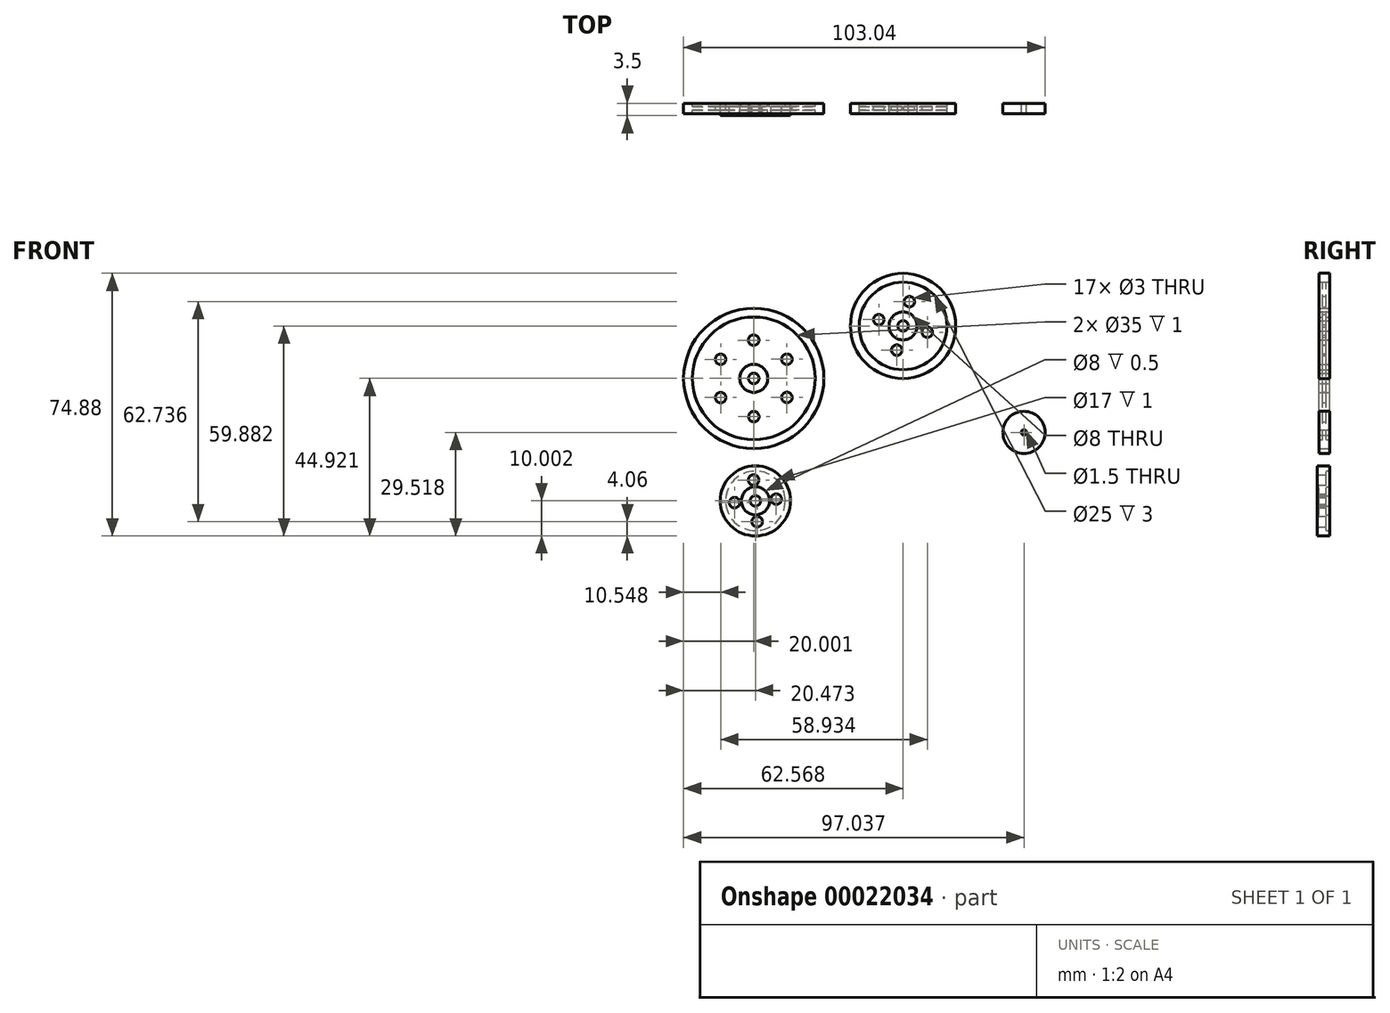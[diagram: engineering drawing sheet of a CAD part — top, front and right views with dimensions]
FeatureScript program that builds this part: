
annotation { "Feature Type Name" : "Feature", "Feature Type Description" : "" }
export const myFeature = defineFeature(function(context is Context, id is Id, definition is map)
    precondition{}
    {
        {
            var Q0;
            Q0=qCreatedBy(makeId("Front.planeOp"),FACE);
            var sketch = newSketch(context, id + "F0", { "sketchPlane" : qUnion([Q0])});
            skCircle(sketch, "E0", {"center": v(-69.05, 21.82) * mm, "radius": 20 * mm});
            skCircle(sketch, "E1", {"center": v(-26.48, 36.78) * mm, "radius": 15 * mm});
            skCircle(sketch, "E2", {"center": v(7.99, 6.42) * mm, "radius": 6 * mm});
            skCircle(sketch, "E3", {"center": v(-69.05, 21.82) * mm, "radius": 4 * mm});
            skCircle(sketch, "E4", {"center": v(-26.48, 36.78) * mm, "radius": 4 * mm});
            skCircle(sketch, "E5", {"center": v(-69.05, 21.82) * mm, "radius": 1.5 * mm});
            skCircle(sketch, "E6", {"center": v(-26.48, 36.78) * mm, "radius": 1.5 * mm});
            skCircle(sketch, "E7", {"center": v(7.99, 6.42) * mm, "radius": 0.75 * mm});
            skCircle(sketch, "E8", {"center": v(-26.48, 36.78) * mm, "radius": 12.5 * mm});
            skCircle(sketch, "E9", {"center": v(-69.05, 21.82) * mm, "radius": 17.5 * mm});
            skCircle(sketch, "E10", {"center": v(7.99, 6.42) * mm, "radius": 5 * mm});
            skCircle(sketch, "E11", {"center": v(-33.4, 38.57) * mm, "radius": 1.5 * mm});
            skLineSegment(sketch, "E12", {"start": v(-26.48, 36.78) * mm, "end": v(-25.8, 38.12) * mm});
            skPoint(sketch, "E13.center.orphan", {"position": v(-31.05, -14.24) * mm});
            skPoint(sketch, "E14.center.orphan", {"position": v(-30.48, -14.24) * mm});
            skPoint(sketch, "E15.center.orphan", {"position": v(-25.16, -22.14) * mm});
            skPoint(sketch, "E16.center.orphan", {"position": v(-24.99, -22.14) * mm});
            skLineSegment(sketch, "E17", {"start": v(-37.52, -14.62) * mm, "end": v(-37.5, -14.63) * mm});
            skLineSegment(sketch, "E18.trimOffspring", {"start": v(-34.31, -17.76) * mm, "end": v(-34.3, -17.78) * mm});
            skPoint(sketch, "E19.end.orphan", {"position": v(-35.63, -17.78) * mm});
            skPoint(sketch, "E20.right.start.orphan", {"position": v(-26.2, -16.2) * mm});
            skCircle(sketch, "E21.1.0", {"center": v(-28.27, 29.87) * mm, "radius": 1.5 * mm});
            skCircle(sketch, "E21.2.0", {"center": v(-19.57, 35) * mm, "radius": 1.5 * mm});
            skCircle(sketch, "E21.3.0", {"center": v(-24.7, 43.7) * mm, "radius": 1.5 * mm});
            skCircle(sketch, "E22.1.0", {"center": v(-69.03, 10.92) * mm, "radius": 1.5 * mm});
            skPoint(sketch, "E23.trimOffspring.end.orphan", {"position": v(-69.05, 26.32) * mm});
            skCircle(sketch, "E24.1.0", {"center": v(-59.6, 16.39) * mm, "radius": 1.5 * mm});
            skCircle(sketch, "E24.2.0", {"center": v(-59.61, 27.3) * mm, "radius": 1.5 * mm});
            skCircle(sketch, "E24.3.0", {"center": v(-69.07, 32.73) * mm, "radius": 1.5 * mm});
            skCircle(sketch, "E24.4.0", {"center": v(-78.5, 27.26) * mm, "radius": 1.5 * mm});
            skCircle(sketch, "E24.5.0", {"center": v(-78.48, 16.35) * mm, "radius": 1.5 * mm});
            skPoint(sketch, "E25.center.orphan", {"position": v(-35.91, -16.2) * mm});
            skPoint(sketch, "E26.end.orphan", {"position": v(-31.05, -11.72) * mm});
            skPoint(sketch, "E26.start.orphan", {"position": v(-31.06, -16.2) * mm});
            skCircle(sketch, "E27", {"center": v(-68.58, -13.1) * mm, "radius": 10 * mm});
            skCircle(sketch, "E28", {"center": v(-68.58, -13.1) * mm, "radius": 8.5 * mm});
            skCircle(sketch, "E29", {"center": v(-68.58, -13.1) * mm, "radius": 4 * mm});
            skCircle(sketch, "E30", {"center": v(-68.58, -13.1) * mm, "radius": 1.5 * mm});
            skCircle(sketch, "E31.1.0", {"center": v(-69.08, -7.16) * mm, "radius": 1.5 * mm});
            skCircle(sketch, "E32.1.0", {"center": v(-74.52, -13.6) * mm, "radius": 1.5 * mm});
            skCircle(sketch, "E32.2.0", {"center": v(-68.07, -19.04) * mm, "radius": 1.5 * mm});
            skCircle(sketch, "E32.3.0", {"center": v(-62.63, -12.6) * mm, "radius": 1.5 * mm});
            skLineSegment(sketch, "E33.trimOffspring", {"start": v(-68.89, -9.11) * mm, "end": v(-68.93, -8.65) * mm});
            skSolve(sketch);
        }
        {
            var Q0;
            Q0=makeQuery(id+"F0.imprint","IMPRINT",FACE,{"disambiguationData":[TD([[makeQuery(id+"F0.imprint","IMPRINT",EDGE,{"derivedFrom":sQuery(id+"F0.wireOp",EDGE,"E1")}),1.0]])]});
            extrude(context, id + "F1", {"entities" : qUnion([Q0]), "endBound" : BoundingType.SYMMETRIC, "depth" : 3 * mm});
        }
        {
            var Q0;
            Q0=makeQuery(id+"F0.imprint","IMPRINT",FACE,{"disambiguationData":[TD([[makeQuery(id+"F0.imprint","IMPRINT",EDGE,{"derivedFrom":sQuery(id+"F0.wireOp",EDGE,"E4")}),1.0]])]});
            extrude(context, id + "F2", {"entities" : qUnion([Q0]), "endBound" : BoundingType.SYMMETRIC, "depth" : 3 * mm});
        }
        {
            var Q0;
            Q0=makeQuery(id+"F0.imprint","IMPRINT",FACE,{"disambiguationData":[TD([[makeQuery(id+"F0.imprint","IMPRINT",EDGE,{"derivedFrom":sQuery(id+"F0.wireOp",EDGE,"E4")}),-1.0]])]});
            extrude(context, id + "F3", {"entities" : qUnion([Q0]), "endBound" : BoundingType.SYMMETRIC, "depth" : 1 * mm});
        }
        {
            var Q0;
            Q0=makeQuery(id+"F0.imprint","IMPRINT",FACE,{"disambiguationData":[TD([[makeQuery(id+"F0.imprint","IMPRINT",EDGE,{"derivedFrom":sQuery(id+"F0.wireOp",EDGE,"E27")}),1.0]])]});
            var Q1;
            Q1=makeQuery(id+"F0.imprint","IMPRINT",FACE,{"disambiguationData":[TD([[makeQuery(id+"F0.imprint","IMPRINT",EDGE,{"derivedFrom":sQuery(id+"F0.wireOp",EDGE,"E28")}),1.0]])]});
            extrude(context, id + "F4", {"entities" : qUnion([Q0, Q1]), "operationType" : NewBodyOperationType.ADD, "depth" : 2 * mm});
        }
        {
            var Q0;
            Q0=makeQuery(id+"F0.imprint","IMPRINT",FACE,{"disambiguationData":[TD([[makeQuery(id+"F0.imprint","IMPRINT",EDGE,{"derivedFrom":sQuery(id+"F0.wireOp",EDGE,"E27")}),1.0]])]});
            var Q1;
            Q1=makeQuery(id+"F0.imprint","IMPRINT",FACE,{"disambiguationData":[TD([[makeQuery(id+"F0.imprint","IMPRINT",EDGE,{"derivedFrom":sQuery(id+"F0.wireOp",EDGE,"E28")}),1.0]])]});
            extrude(context, id + "F5", {"entities" : qUnion([Q0, Q1]), "operationType" : NewBodyOperationType.ADD, "endBound" : BoundingType.SYMMETRIC, "depth" : 1 * mm});
        }
        {
            var Q0;
            Q0=makeQuery(id+"F0.imprint","IMPRINT",FACE,{"disambiguationData":[TD([[makeQuery(id+"F0.imprint","IMPRINT",EDGE,{"derivedFrom":sQuery(id+"F0.wireOp",EDGE,"E28")}),1.0]])]});
            extrude(context, id + "F6", {"entities" : qUnion([Q0]), "endBound" : BoundingType.SYMMETRIC, "depth" : 1 * mm});
        }
        {
            var Q0;
            Q0=makeQuery(id+"F0.imprint","IMPRINT",FACE,{"disambiguationData":[TD([[makeQuery(id+"F0.imprint","IMPRINT",EDGE,{"derivedFrom":sQuery(id+"F0.wireOp",EDGE,"E27")}),1.0]])]});
            extrude(context, id + "F7", {"entities" : qUnion([Q0]), "operationType" : NewBodyOperationType.ADD, "endBound" : BoundingType.SYMMETRIC, "depth" : 3 * mm});
        }
        {
            var Q0;
            Q0=makeQuery(id+"F0.imprint","IMPRINT",FACE,{"disambiguationData":[TD([[makeQuery(id+"F0.imprint","IMPRINT",EDGE,{"derivedFrom":sQuery(id+"F0.wireOp",EDGE,"E29")}),1.0]])]});
            extrude(context, id + "F8", {"entities" : qUnion([Q0]), "operationType" : NewBodyOperationType.ADD, "endBound" : BoundingType.SYMMETRIC, "depth" : 3 * mm});
        }
        {
            var Q0;
            Q0=makeQuery(id+"F0.imprint","IMPRINT",FACE,{"disambiguationData":[TD([[makeQuery(id+"F0.imprint","IMPRINT",EDGE,{"derivedFrom":sQuery(id+"F0.wireOp",EDGE,"E3")}),-1.0]])]});
            extrude(context, id + "F9", {"entities" : qUnion([Q0]), "operationType" : NewBodyOperationType.ADD, "endBound" : BoundingType.SYMMETRIC, "depth" : 1 * mm});
        }
        {
            var Q0;
            Q0=makeQuery(id+"F0.imprint","IMPRINT",FACE,{"disambiguationData":[TD([[makeQuery(id+"F0.imprint","IMPRINT",EDGE,{"derivedFrom":sQuery(id+"F0.wireOp",EDGE,"E3")}),1.0]])]});
            extrude(context, id + "F10", {"entities" : qUnion([Q0]), "operationType" : NewBodyOperationType.ADD, "endBound" : BoundingType.SYMMETRIC, "depth" : 3 * mm});
        }
        {
            var Q0;
            Q0=makeQuery(id+"F0.imprint","IMPRINT",FACE,{"disambiguationData":[TD([[makeQuery(id+"F0.imprint","IMPRINT",EDGE,{"derivedFrom":sQuery(id+"F0.wireOp",EDGE,"E0")}),1.0]])]});
            extrude(context, id + "F11", {"entities" : qUnion([Q0]), "endBound" : BoundingType.SYMMETRIC, "depth" : 3 * mm});
        }
        {
            var Q0;
            Q0=makeQuery(id+"F0.imprint","IMPRINT",FACE,{"disambiguationData":[TD([[makeQuery(id+"F0.imprint","IMPRINT",EDGE,{"derivedFrom":sQuery(id+"F0.wireOp",EDGE,"E3")}),-1.0]])]});
            extrude(context, id + "F12", {"entities" : qUnion([Q0]), "operationType" : NewBodyOperationType.ADD, "endBound" : BoundingType.SYMMETRIC, "depth" : 1 * mm});
        }
        {
            var Q0;
            Q0=makeQuery(id+"F0.imprint","IMPRINT",FACE,{"disambiguationData":[TD([[makeQuery(id+"F0.imprint","IMPRINT",EDGE,{"derivedFrom":sQuery(id+"F0.wireOp",EDGE,"E3")}),1.0]])]});
            extrude(context, id + "F13", {"entities" : qUnion([Q0]), "operationType" : NewBodyOperationType.ADD, "endBound" : BoundingType.SYMMETRIC, "depth" : 3 * mm});
        }
        {
            var Q0;
            Q0=makeQuery(id+"F0.imprint","IMPRINT",FACE,{"disambiguationData":[TD([[makeQuery(id+"F0.imprint","IMPRINT",EDGE,{"derivedFrom":sQuery(id+"F0.wireOp",EDGE,"E2")}),1.0]])]});
            var Q1;
            Q1=makeQuery(id+"F0.imprint","IMPRINT",FACE,{"disambiguationData":[TD([[makeQuery(id+"F0.imprint","IMPRINT",EDGE,{"derivedFrom":sQuery(id+"F0.wireOp",EDGE,"E7")}),-1.0]])]});
            extrude(context, id + "F14", {"entities" : qUnion([Q0, Q1]), "endBound" : BoundingType.SYMMETRIC, "depth" : 3 * mm});
        }
    });
